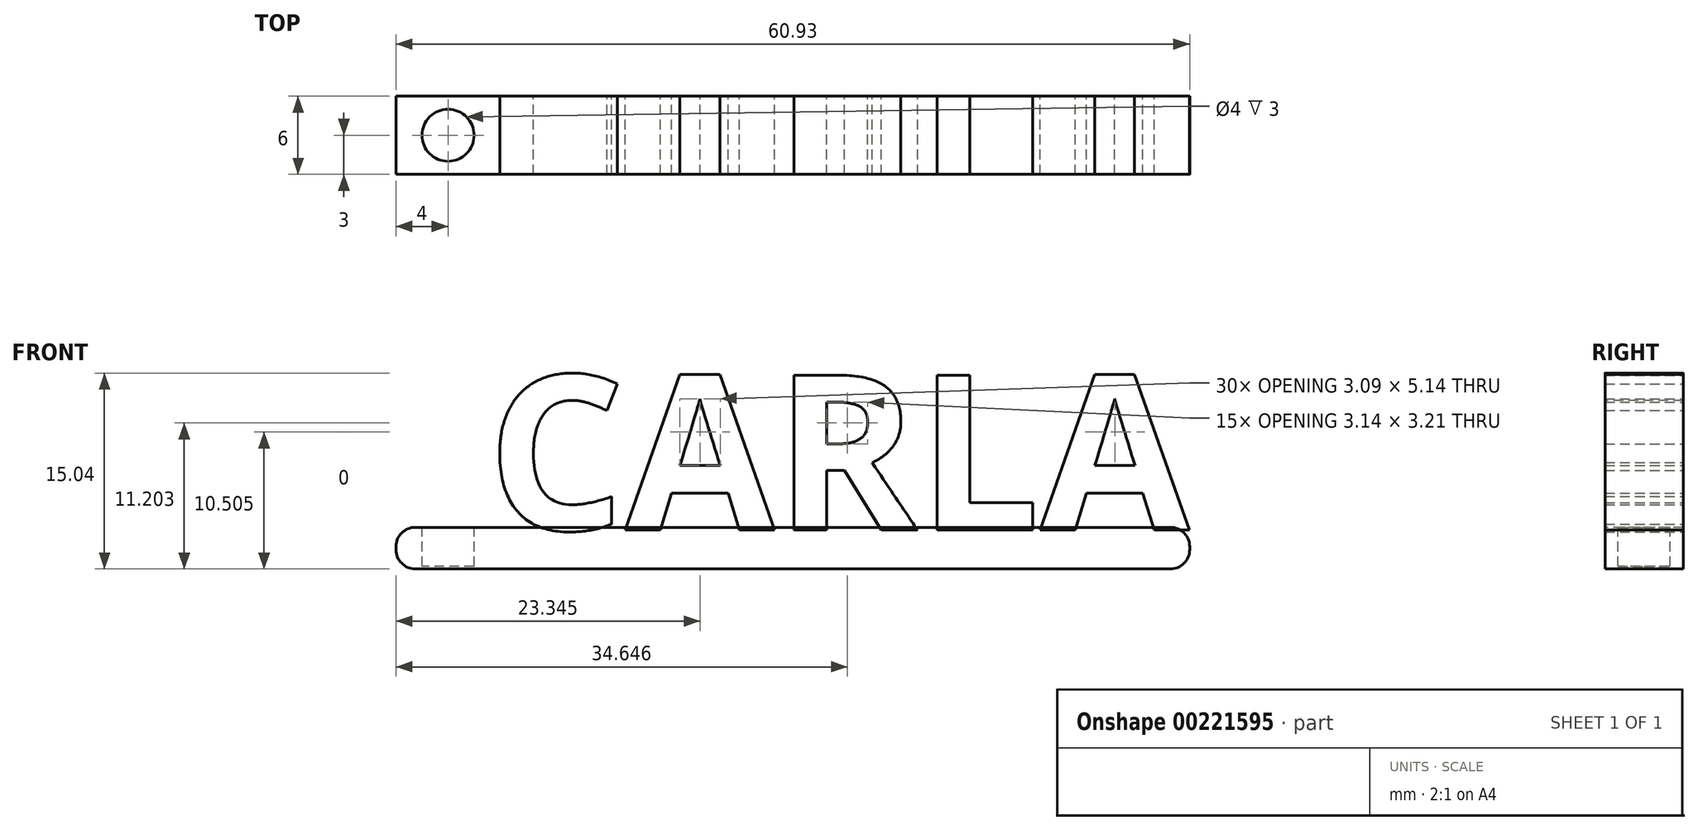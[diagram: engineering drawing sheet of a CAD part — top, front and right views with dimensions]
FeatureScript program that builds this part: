
annotation { "Feature Type Name" : "Feature", "Feature Type Description" : "" }
export const myFeature = defineFeature(function(context is Context, id is Id, definition is map)
    precondition{}
    {
        {
            var Q0;
            Q0=qCreatedBy(makeId("Front.planeOp"),FACE);
            var sketch = newSketch(context, id + "F0", { "sketchPlane" : qUnion([Q0])});
            skText(sketch, "E0", { "text": "CARLA", "fontName": "OpenSans-Bold.ttf"});
            const initialGuessF0  = {"E0": [-0.02, 0, 1, 0, 0.01197]};
            skSetInitialGuess(sketch, initialGuessF0);
            skSolve(sketch);
        }
        {
            var Q0;
            Q0=qSketchRegion(id+"F0",true);
            extrude(context, id + "F1", {"entities" : qUnion([Q0]), "endBound" : BoundingType.SYMMETRIC, "depth" : 6 * mm});
        }
        {
            var Q0;
            Q0=qCreatedBy(makeId("Top.planeOp"),FACE);
            var sketch = newSketch(context, id + "F2", { "sketchPlane" : qUnion([Q0])});
            skLineSegment(sketch, "E1.bottom", {"start": v(-20, 3) * mm, "end": v(33.93, 3) * mm});
            skLineSegment(sketch, "E1.top", {"start": v(-20, -3) * mm, "end": v(33.93, -3) * mm});
            skLineSegment(sketch, "E1.left", {"start": v(-20, 3) * mm, "end": v(-20, -3) * mm});
            skLineSegment(sketch, "E1.right", {"start": v(33.93, 3) * mm, "end": v(33.93, -3) * mm});
            skSolve(sketch);
        }
        {
            var Q0;
            Q0=makeQuery(id+"F2.imprint","IMPRINT",FACE,{"disambiguationData":[TD([[makeQuery(id+"F2.imprint","IMPRINT",EDGE,{"derivedFrom":sQuery(id+"F2.wireOp",EDGE,"E1.bottom")}),-1.0]])]});
            extrude(context, id + "F3", {"entities" : qUnion([Q0]), "depth" : 0.2 * mm});
        }
        {
            var Q0;
            Q0=makeQuery(id+"F3.opExtrude","CAP_FACE",FACE,{"disambiguationData":[OSD([sQuery(id+"F2.wireOp",EDGE,"E1.bottom"),sQuery(id+"F2.wireOp",EDGE,"E1.top"),sQuery(id+"F2.wireOp",EDGE,"E1.left"),sQuery(id+"F2.wireOp",EDGE,"E1.right")])],"isStart":true});
            extrude(context, id + "F4", {"entities" : qUnion([Q0]), "depth" : 3 * mm});
        }
        {
            var Q0;
            {var subQ0=sQuery(id+"F2.wireOp",EDGE,"E1.left");Q0=makeQuery(id+"FaVoHrOpcFZXiYX_6.opBoolean","MERGE",FACE,{"derivedFrom":[makeQuery(id+"F3.opExtrude","SWEPT_FACE",FACE,{"disambiguationData":[OSD([subQ0])]}),makeQuery(id+"F4.opExtrude","SWEPT_FACE",FACE,{"disambiguationData":[OSD([subQ0])]})]});}
            var sketch = newSketch(context, id + "F5", { "sketchPlane" : qUnion([Q0])});
            skLineSegment(sketch, "E2.bottom", {"start": v(-3, -3) * mm, "end": v(3, -3) * mm});
            skLineSegment(sketch, "E2.top", {"start": v(-3, 0.2) * mm, "end": v(3, 0.2) * mm});
            skLineSegment(sketch, "E2.left", {"start": v(-3, -3) * mm, "end": v(-3, 0.2) * mm});
            skLineSegment(sketch, "E2.right", {"start": v(3, -3) * mm, "end": v(3, 0.2) * mm});
            skSolve(sketch);
        }
        {
            var Q0;
            Q0=qSketchRegion(id+"F5",true);
            extrude(context, id + "F6", {"entities" : qUnion([Q0]), "operationType" : NewBodyOperationType.ADD, "depth" : 7 * mm});
        }
        {
            var Q0;
            Q0=makeQuery(id+"F6.opExtrude","CAP_EDGE",EDGE,{"disambiguationData":[OSD([sQuery(id+"F5.wireOp",EDGE,"E2.bottom")])],"isStart":false});
            var Q1;
            Q1=makeQuery(id+"F6.opExtrude","CAP_EDGE",EDGE,{"disambiguationData":[OSD([sQuery(id+"F5.wireOp",EDGE,"E2.top")])],"isStart":false});
            var Q2;
            Q2=makeQuery(id+"F4.opExtrude","CAP_EDGE",EDGE,{"disambiguationData":[OSD([sQuery(id+"F2.wireOp",EDGE,"E1.right")])],"isStart":false});
            var Q3;
            Q3=makeQuery(id+"F3.opExtrude","CAP_EDGE",EDGE,{"disambiguationData":[OSD([sQuery(id+"F2.wireOp",EDGE,"E1.right")])],"isStart":false});
            fillet(context, id + "F7", {"entities" : qUnion([Q0, Q1, Q2, Q3]), "radius" : 1.5 * mm, "tangentPropagation" : true, "allowEdgeOverflow" : false});
        }
        {
            var Q0;
            {var subQ19=sQuery(id+"F2.wireOp",EDGE,"E1.top");var subQ20=sQuery(id+"F2.wireOp",EDGE,"E1.bottom");var subQ63=sQuery(id+"F0.wireOp",EDGE,"E0.sketch_text.stroke-2");var subQ66=sQuery(id+"F2.wireOp",EDGE,"E1.left");Q0=makeQuery(id+"F6.boolean.opBoolean","MERGE",FACE,{"derivedFrom":[makeQuery(id+"FaVoHrOpcFZXiYX_6.opBoolean","SPLIT",FACE,{"disambiguationData":[TD([makeQuery(id+"F1.opExtrude","SWEPT_FACE",FACE,{"disambiguationData":[OSD([subQ63])]})])],"derivedFrom":makeQuery(id+"F3.opExtrude","CAP_FACE",FACE,{"disambiguationData":[OSD([subQ20,subQ19,subQ66,sQuery(id+"F2.wireOp",EDGE,"E1.right")])],"isStart":false})}),makeQuery(id+"F6.opExtrude","SWEPT_FACE",FACE,{"disambiguationData":[OSD([sQuery(id+"F5.wireOp",EDGE,"E2.top")])]})]});}
            var sketch = newSketch(context, id + "F8", { "sketchPlane" : qUnion([Q0])});
            skCircle(sketch, "E3", {"center": v(-23, 0) * mm, "radius": 2 * mm});
            skSolve(sketch);
        }
        {
            var Q0;
            Q0=makeQuery(id+"F8.imprint","IMPRINT",FACE,{"disambiguationData":[TD([[makeQuery(id+"F8.imprint","IMPRINT",EDGE,{"derivedFrom":sQuery(id+"F8.wireOp",EDGE,"E3")}),1.0]])]});
            extrude(context, id + "F9", {"entities" : qUnion([Q0]), "operationType" : NewBodyOperationType.REMOVE, "oppositeDirection" : true, "depth" : 3 * mm});
        }
    });
